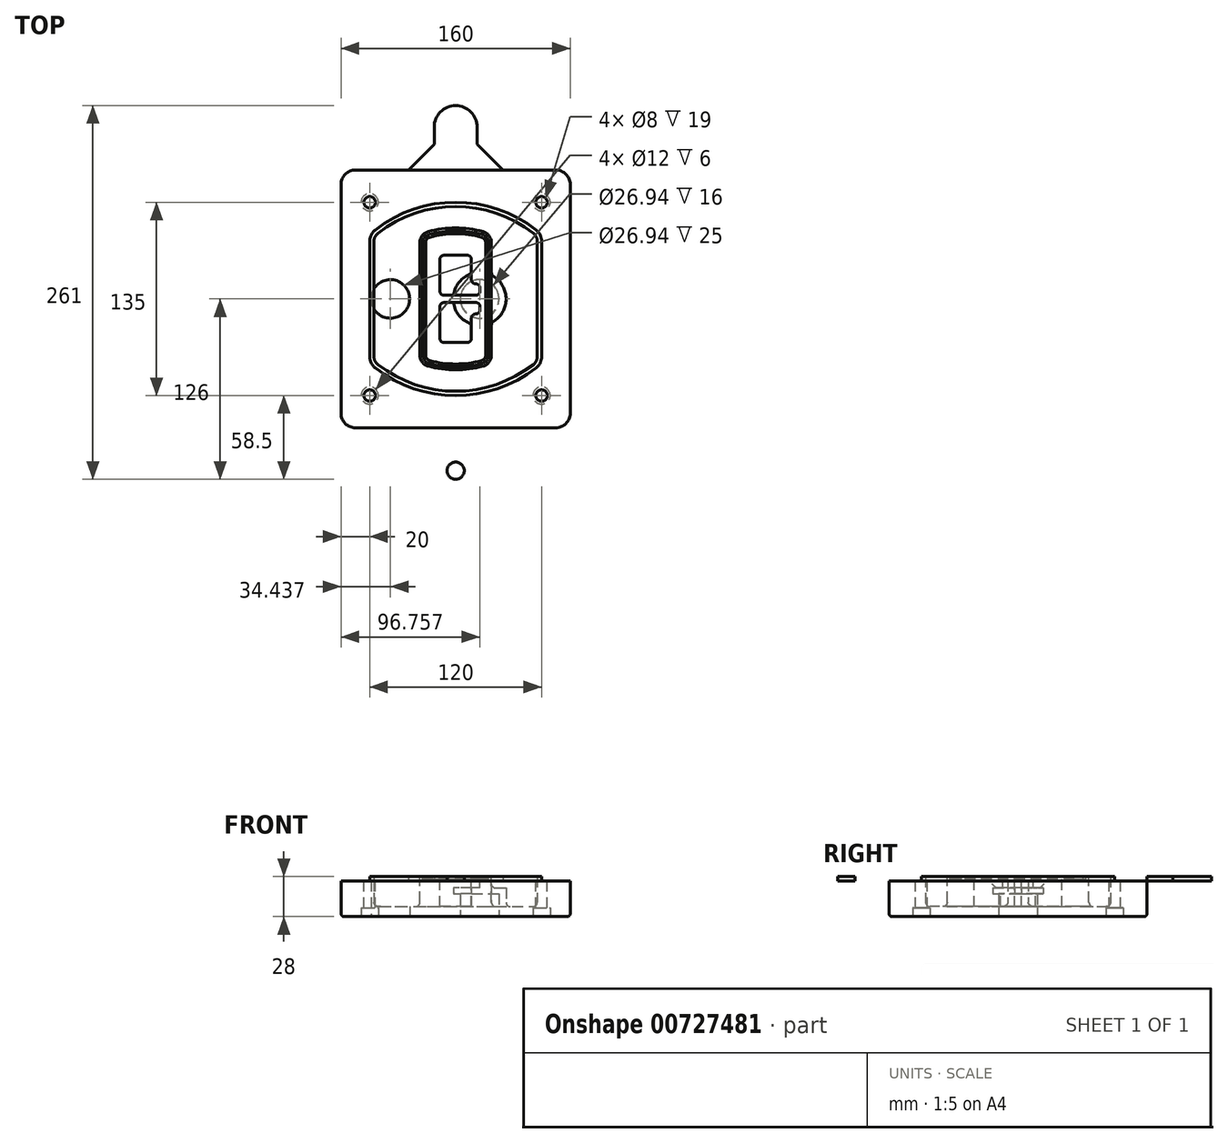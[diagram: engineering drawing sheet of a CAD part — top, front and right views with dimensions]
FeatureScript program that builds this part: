
annotation { "Feature Type Name" : "Feature", "Feature Type Description" : "" }
export const myFeature = defineFeature(function(context is Context, id is Id, definition is map)
    precondition{}
    {
        {
            var Q0;
            Q0=qCreatedBy(makeId("Top.planeOp"),FACE);
            var sketch = newSketch(context, id + "F0", { "sketchPlane" : qUnion([Q0])});
            skPoint(sketch, "E0.rect.middle", {"position": v(0, 0) * mm});
            skLineSegment(sketch, "E1.bottom", {"start": v(-70, -90) * mm, "end": v(70, -90) * mm});
            skLineSegment(sketch, "E1.top", {"start": v(-70, 90) * mm, "end": v(70, 90) * mm});
            skLineSegment(sketch, "E1.left", {"start": v(-80, -80) * mm, "end": v(-80, 80) * mm});
            skLineSegment(sketch, "E1.right", {"start": v(80, -80) * mm, "end": v(80, 80) * mm});
            skLineSegment(sketch, "E2", {"start": v(-80, 90) * mm, "end": v(80, -90) * mm, "construction": true});
            skLineSegment(sketch, "E3", {"start": v(80, 90) * mm, "end": v(-80, -90) * mm, "construction": true});
            skCircle(sketch, "E4", {"center": v(-60, 67.5) * mm, "radius": 4 * mm});
            skCircle(sketch, "E5", {"center": v(60, 67.5) * mm, "radius": 4 * mm});
            skCircle(sketch, "E6", {"center": v(60, -67.5) * mm, "radius": 4 * mm});
            skCircle(sketch, "E7", {"center": v(-60, -67.5) * mm, "radius": 4 * mm});
            skLineSegment(sketch, "E8", {"start": v(-60, 67.5) * mm, "end": v(60, 67.5) * mm, "construction": true});
            skLineSegment(sketch, "E9", {"start": v(60, 67.5) * mm, "end": v(60, -67.5) * mm, "construction": true});
            skLineSegment(sketch, "E10", {"start": v(60, -67.5) * mm, "end": v(-60, -67.5) * mm, "construction": true});
            skLineSegment(sketch, "E11", {"start": v(-60, -67.5) * mm, "end": v(-60, 67.5) * mm, "construction": true});
            skLineSegment(sketch, "E12", {"start": v(-60, 40.3) * mm, "end": v(-60, -40.3) * mm});
            skLineSegment(sketch, "E13", {"start": v(60, 40.3) * mm, "end": v(60, -40.3) * mm});
            skArc(sketch, "E14", {"start": v(56.15, 48.18) * mm, "mid": v(0, 67.5) * mm, "end": v(-56.15, 48.18) * mm});
            skArc(sketch, "E15", {"start": v(-56.15, -48.18) * mm, "mid": v(0, -67.5) * mm, "end": v(56.15, -48.18) * mm});
            skLineSegment(sketch, "E16", {"start": v(-60, 0) * mm, "end": v(60, 0) * mm, "construction": true});
            skPoint(sketch, "E17.visualSharp", {"position": v(-60, -45) * mm});
            skArc(sketch, "E17.filletArc", {"start": v(-60, -40.3) * mm, "mid": v(-58.99, -44.68) * mm, "end": v(-56.15, -48.18) * mm});
            skPoint(sketch, "E18.visualSharp", {"position": v(-60, 45) * mm});
            skArc(sketch, "E18.filletArc", {"start": v(-56.15, 48.18) * mm, "mid": v(-58.99, 44.68) * mm, "end": v(-60, 40.3) * mm});
            skPoint(sketch, "E19.visualSharp", {"position": v(60, 45) * mm});
            skArc(sketch, "E19.filletArc", {"start": v(60, 40.3) * mm, "mid": v(58.99, 44.68) * mm, "end": v(56.15, 48.18) * mm});
            skPoint(sketch, "E20.visualSharp", {"position": v(60, -45) * mm});
            skArc(sketch, "E20.filletArc", {"start": v(56.15, -48.18) * mm, "mid": v(58.99, -44.68) * mm, "end": v(60, -40.3) * mm});
            skPoint(sketch, "E21.visualSharp", {"position": v(-80, 90) * mm});
            skArc(sketch, "E21.filletArc", {"start": v(-70, 90) * mm, "mid": v(-77.07, 87.07) * mm, "end": v(-80, 80) * mm});
            skPoint(sketch, "E22.visualSharp", {"position": v(80, 90) * mm});
            skArc(sketch, "E22.filletArc", {"start": v(80, 80) * mm, "mid": v(77.07, 87.07) * mm, "end": v(70, 90) * mm});
            skPoint(sketch, "E23.visualSharp", {"position": v(80, -90) * mm});
            skArc(sketch, "E23.filletArc", {"start": v(70, -90) * mm, "mid": v(77.07, -87.07) * mm, "end": v(80, -80) * mm});
            skPoint(sketch, "E24.visualSharp", {"position": v(-80, -90) * mm});
            skArc(sketch, "E24.filletArc", {"start": v(-80, -80) * mm, "mid": v(-77.07, -87.07) * mm, "end": v(-70, -90) * mm});
            skArc(sketch, "E25.0", {"start": v(57, 40.3) * mm, "mid": v(56.3, 43.36) * mm, "end": v(54.3, 45.81) * mm});
            skLineSegment(sketch, "E25.1", {"start": v(57, 40.3) * mm, "end": v(57, -40.3) * mm});
            skArc(sketch, "E25.2", {"start": v(54.3, -45.81) * mm, "mid": v(56.3, -43.36) * mm, "end": v(57, -40.3) * mm});
            skArc(sketch, "E25.3", {"start": v(-54.3, -45.81) * mm, "mid": v(0, -64.5) * mm, "end": v(54.3, -45.81) * mm});
            skArc(sketch, "E25.4", {"start": v(-57, -40.3) * mm, "mid": v(-56.3, -43.36) * mm, "end": v(-54.3, -45.81) * mm});
            skArc(sketch, "E25.5", {"start": v(54.3, 45.81) * mm, "mid": v(0, 64.5) * mm, "end": v(-54.3, 45.81) * mm});
            skLineSegment(sketch, "E25.6", {"start": v(-57, 40.3) * mm, "end": v(-57, -40.3) * mm});
            skArc(sketch, "E25.7", {"start": v(-54.3, 45.81) * mm, "mid": v(-56.3, 43.36) * mm, "end": v(-57, 40.3) * mm});
            skArc(sketch, "E26.0", {"start": v(-58.62, 51.33) * mm, "mid": v(-62.58, 46.43) * mm, "end": v(-64, 40.3) * mm});
            skArc(sketch, "E26.1", {"start": v(58.62, 51.33) * mm, "mid": v(0, 71.5) * mm, "end": v(-58.62, 51.33) * mm});
            skArc(sketch, "E26.2", {"start": v(64, 40.3) * mm, "mid": v(62.58, 46.43) * mm, "end": v(58.62, 51.33) * mm});
            skLineSegment(sketch, "E26.3", {"start": v(64, 40.3) * mm, "end": v(64, -40.3) * mm});
            skArc(sketch, "E26.4", {"start": v(58.62, -51.33) * mm, "mid": v(62.58, -46.43) * mm, "end": v(64, -40.3) * mm});
            skLineSegment(sketch, "E26.5", {"start": v(-64, 40.3) * mm, "end": v(-64, -40.3) * mm});
            skArc(sketch, "E26.6", {"start": v(-58.62, -51.33) * mm, "mid": v(0, -71.5) * mm, "end": v(58.62, -51.33) * mm});
            skArc(sketch, "E26.7", {"start": v(-64, -40.3) * mm, "mid": v(-62.58, -46.43) * mm, "end": v(-58.62, -51.33) * mm});
            skSolve(sketch);
        }
        {
            var Q0;
            Q0=makeQuery(id+"F0.imprint","IMPRINT",FACE,{"disambiguationData":[TD([[makeQuery(id+"F0.imprint","IMPRINT",EDGE,{"derivedFrom":sQuery(id+"F0.wireOp",EDGE,"E1.bottom")}),1.0]])]});
            var Q1;
            Q1=makeQuery(id+"F0.imprint","IMPRINT",FACE,{"disambiguationData":[TD([[makeQuery(id+"F0.imprint","IMPRINT",EDGE,{"derivedFrom":sQuery(id+"F0.wireOp",EDGE,"E12")}),1.0]])]});
            var Q2;
            Q2=makeQuery(id+"F0.imprint","IMPRINT",FACE,{"disambiguationData":[TD([[makeQuery(id+"F0.imprint","IMPRINT",EDGE,{"derivedFrom":sQuery(id+"F0.wireOp",EDGE,"E25.0")}),1.0]])]});
            var Q3;
            Q3=makeQuery(id+"F0.imprint","IMPRINT",FACE,{"disambiguationData":[TD([[makeQuery(id+"F0.imprint","IMPRINT",EDGE,{"derivedFrom":sQuery(id+"F0.wireOp",EDGE,"E12")}),-1.0]])]});
            extrude(context, id + "F1", {"entities" : qUnion([Q0, Q1, Q2, Q3]), "oppositeDirection" : true, "depth" : 25 * mm});
        }
        {
            var Q0;
            Q0=makeQuery(id+"F0.imprint","IMPRINT",FACE,{"disambiguationData":[TD([[makeQuery(id+"F0.imprint","IMPRINT",EDGE,{"derivedFrom":sQuery(id+"F0.wireOp",EDGE,"E12")}),1.0]])]});
            extrude(context, id + "F2", {"entities" : qUnion([Q0]), "operationType" : NewBodyOperationType.ADD, "depth" : 3 * mm});
        }
        {
            var Q0;
            Q0=makeQuery(id+"F0.imprint","IMPRINT",FACE,{"disambiguationData":[TD([[makeQuery(id+"F0.imprint","IMPRINT",EDGE,{"derivedFrom":sQuery(id+"F0.wireOp",EDGE,"E25.0")}),1.0]])]});
            extrude(context, id + "F3", {"entities" : qUnion([Q0]), "operationType" : NewBodyOperationType.REMOVE, "oppositeDirection" : true, "depth" : 18 * mm});
        }
        {
            var Q0;
            Q0=makeQuery(id+"F2.opExtrude","CAP_FACE",FACE,{"disambiguationData":[OSD([sQuery(id+"F0.wireOp",EDGE,"E12"),sQuery(id+"F0.wireOp",EDGE,"E13"),sQuery(id+"F0.wireOp",EDGE,"E14"),sQuery(id+"F0.wireOp",EDGE,"E15"),sQuery(id+"F0.wireOp",EDGE,"E17.filletArc"),sQuery(id+"F0.wireOp",EDGE,"E18.filletArc"),sQuery(id+"F0.wireOp",EDGE,"E19.filletArc"),sQuery(id+"F0.wireOp",EDGE,"E20.filletArc"),sQuery(id+"F0.wireOp",EDGE,"E25.0"),sQuery(id+"F0.wireOp",EDGE,"E25.1"),sQuery(id+"F0.wireOp",EDGE,"E25.2"),sQuery(id+"F0.wireOp",EDGE,"E25.3"),sQuery(id+"F0.wireOp",EDGE,"E25.4"),sQuery(id+"F0.wireOp",EDGE,"E25.5"),sQuery(id+"F0.wireOp",EDGE,"E25.6"),sQuery(id+"F0.wireOp",EDGE,"E25.7")])],"isStart":false});
            var sketch = newSketch(context, id + "F4", { "sketchPlane" : qUnion([Q0])});
            skArc(sketch, "E27.0", {"start": v(-19.08, -46.97) * mm, "mid": v(0, -49.5) * mm, "end": v(19.08, -46.97) * mm});
            skArc(sketch, "E28.0", {"start": v(19.08, 46.97) * mm, "mid": v(0, 49.5) * mm, "end": v(-19.08, 46.97) * mm});
            skLineSegment(sketch, "E29", {"start": v(-25, 39.25) * mm, "end": v(-25, -39.25) * mm});
            skLineSegment(sketch, "E30", {"start": v(25, 39.25) * mm, "end": v(25, -39.25) * mm});
            skLineSegment(sketch, "E31", {"start": v(-25, 45.1) * mm, "end": v(25, 45.1) * mm, "construction": true});
            skLineSegment(sketch, "E32", {"start": v(-25, -45.1) * mm, "end": v(25, -45.1) * mm, "construction": true});
            skPoint(sketch, "E33.visualSharp", {"position": v(-25, 45.1) * mm});
            skArc(sketch, "E33.filletArc", {"start": v(-19.08, 46.97) * mm, "mid": v(-23.35, 44.11) * mm, "end": v(-25, 39.25) * mm});
            skPoint(sketch, "E34.visualSharp", {"position": v(25, 45.1) * mm});
            skArc(sketch, "E34.filletArc", {"start": v(25, 39.25) * mm, "mid": v(23.35, 44.11) * mm, "end": v(19.08, 46.97) * mm});
            skPoint(sketch, "E35.visualSharp", {"position": v(25, -45.1) * mm});
            skArc(sketch, "E35.filletArc", {"start": v(19.08, -46.97) * mm, "mid": v(23.35, -44.11) * mm, "end": v(25, -39.25) * mm});
            skPoint(sketch, "E36.visualSharp", {"position": v(-25, -45.1) * mm});
            skArc(sketch, "E36.filletArc", {"start": v(-25, -39.25) * mm, "mid": v(-23.35, -44.11) * mm, "end": v(-19.08, -46.97) * mm});
            skArc(sketch, "E37.0", {"start": v(54.3, 45.81) * mm, "mid": v(0, 64.5) * mm, "end": v(-54.3, 45.81) * mm});
            skArc(sketch, "E37.1", {"start": v(-54.3, 45.81) * mm, "mid": v(-56.3, 43.36) * mm, "end": v(-57, 40.3) * mm});
            skLineSegment(sketch, "E37.2", {"start": v(-57, 40.3) * mm, "end": v(-57, -40.3) * mm});
            skArc(sketch, "E37.3", {"start": v(-57, -40.3) * mm, "mid": v(-56.3, -43.36) * mm, "end": v(-54.3, -45.81) * mm});
            skArc(sketch, "E37.4", {"start": v(-54.3, -45.81) * mm, "mid": v(0, -64.5) * mm, "end": v(54.3, -45.81) * mm});
            skArc(sketch, "E37.5", {"start": v(54.3, -45.81) * mm, "mid": v(56.3, -43.36) * mm, "end": v(57, -40.3) * mm});
            skLineSegment(sketch, "E37.6", {"start": v(57, 40.3) * mm, "end": v(57, -40.3) * mm});
            skArc(sketch, "E37.7", {"start": v(57, 40.3) * mm, "mid": v(56.3, 43.36) * mm, "end": v(54.3, 45.81) * mm});
            skLineSegment(sketch, "E38.0", {"start": v(23, 39.25) * mm, "end": v(23, -39.25) * mm});
            skArc(sketch, "E38.1", {"start": v(18.56, -45.04) * mm, "mid": v(21.76, -42.9) * mm, "end": v(23, -39.25) * mm});
            skArc(sketch, "E38.2", {"start": v(-18.56, -45.04) * mm, "mid": v(0, -47.5) * mm, "end": v(18.56, -45.04) * mm});
            skArc(sketch, "E38.3", {"start": v(-23, -39.25) * mm, "mid": v(-21.76, -42.9) * mm, "end": v(-18.56, -45.04) * mm});
            skLineSegment(sketch, "E38.4", {"start": v(-23, 39.25) * mm, "end": v(-23, -39.25) * mm});
            skArc(sketch, "E38.5", {"start": v(23, 39.25) * mm, "mid": v(21.76, 42.9) * mm, "end": v(18.56, 45.04) * mm});
            skArc(sketch, "E38.6", {"start": v(-18.56, 45.04) * mm, "mid": v(-21.76, 42.9) * mm, "end": v(-23, 39.25) * mm});
            skArc(sketch, "E38.7", {"start": v(18.56, 45.04) * mm, "mid": v(0, 47.5) * mm, "end": v(-18.56, 45.04) * mm});
            skArc(sketch, "E39.0", {"start": v(21, 39.25) * mm, "mid": v(20.18, 41.68) * mm, "end": v(18.04, 43.1) * mm});
            skLineSegment(sketch, "E39.1", {"start": v(21, 39.25) * mm, "end": v(21, -39.25) * mm});
            skArc(sketch, "E39.2", {"start": v(18.04, -43.1) * mm, "mid": v(20.18, -41.68) * mm, "end": v(21, -39.25) * mm});
            skArc(sketch, "E39.3", {"start": v(-18.04, -43.1) * mm, "mid": v(0, -45.5) * mm, "end": v(18.04, -43.1) * mm});
            skArc(sketch, "E39.4", {"start": v(-21, -39.25) * mm, "mid": v(-20.18, -41.68) * mm, "end": v(-18.04, -43.1) * mm});
            skArc(sketch, "E39.5", {"start": v(18.04, 43.1) * mm, "mid": v(0, 45.5) * mm, "end": v(-18.04, 43.1) * mm});
            skLineSegment(sketch, "E39.6", {"start": v(-21, 39.25) * mm, "end": v(-21, -39.25) * mm});
            skArc(sketch, "E39.7", {"start": v(-18.04, 43.1) * mm, "mid": v(-20.18, 41.68) * mm, "end": v(-21, 39.25) * mm});
            skLineSegment(sketch, "E40", {"start": v(-25, 0) * mm, "end": v(25, 0) * mm, "construction": true});
            skLineSegment(sketch, "E41", {"start": v(-11, 5.5) * mm, "end": v(-11, 27.5) * mm});
            skLineSegment(sketch, "E42", {"start": v(-8, 30.5) * mm, "end": v(8, 30.5) * mm});
            skLineSegment(sketch, "E43", {"start": v(11, 27.5) * mm, "end": v(11, 13.5) * mm});
            skLineSegment(sketch, "E44", {"start": v(14, 10.5) * mm, "end": v(14, 10.5) * mm});
            skLineSegment(sketch, "E45", {"start": v(17, 7.5) * mm, "end": v(17, 5.5) * mm});
            skLineSegment(sketch, "E46", {"start": v(14, 2.5) * mm, "end": v(-8, 2.5) * mm});
            skPoint(sketch, "E47.visualSharp", {"position": v(-11, 30.5) * mm});
            skArc(sketch, "E47.filletArc", {"start": v(-8, 30.5) * mm, "mid": v(-10.12, 29.62) * mm, "end": v(-11, 27.5) * mm});
            skPoint(sketch, "E48.visualSharp", {"position": v(11, 30.5) * mm});
            skArc(sketch, "E48.filletArc", {"start": v(11, 27.5) * mm, "mid": v(10.12, 29.62) * mm, "end": v(8, 30.5) * mm});
            skPoint(sketch, "E49.visualSharp", {"position": v(11, 10.5) * mm});
            skArc(sketch, "E49.filletArc", {"start": v(11, 13.5) * mm, "mid": v(11.88, 11.38) * mm, "end": v(14, 10.5) * mm});
            skPoint(sketch, "E50.visualSharp", {"position": v(17, 10.5) * mm});
            skArc(sketch, "E50.filletArc", {"start": v(17, 7.5) * mm, "mid": v(16.12, 9.62) * mm, "end": v(14, 10.5) * mm});
            skPoint(sketch, "E51.visualSharp", {"position": v(17, 2.5) * mm});
            skArc(sketch, "E51.filletArc", {"start": v(14, 2.5) * mm, "mid": v(16.12, 3.38) * mm, "end": v(17, 5.5) * mm});
            skPoint(sketch, "E52.visualSharp", {"position": v(-11, 2.5) * mm});
            skArc(sketch, "E52.filletArc", {"start": v(-11, 5.5) * mm, "mid": v(-10.12, 3.38) * mm, "end": v(-8, 2.5) * mm});
            skLineSegment(sketch, "E53.0.MirrorCS", {"start": v(14, -2.5) * mm, "end": v(-8, -2.5) * mm});
            skArc(sketch, "E54.0.MirrorCS", {"start": v(-11, -5.5) * mm, "mid": v(-10.12, -3.38) * mm, "end": v(-8, -2.5) * mm});
            skLineSegment(sketch, "E55.0.MirrorCS", {"start": v(-11, -5.5) * mm, "end": v(-11, -27.5) * mm});
            skArc(sketch, "E56.0.MirrorCS", {"start": v(-8, -30.5) * mm, "mid": v(-10.12, -29.62) * mm, "end": v(-11, -27.5) * mm});
            skLineSegment(sketch, "E57.0.MirrorCS", {"start": v(-8, -30.5) * mm, "end": v(8, -30.5) * mm});
            skArc(sketch, "E58.0.MirrorCS", {"start": v(11, -27.5) * mm, "mid": v(10.12, -29.62) * mm, "end": v(8, -30.5) * mm});
            skLineSegment(sketch, "E59.0.MirrorCS", {"start": v(11, -27.5) * mm, "end": v(11, -13.5) * mm});
            skArc(sketch, "E60.0.MirrorCS", {"start": v(11, -13.5) * mm, "mid": v(11.88, -11.38) * mm, "end": v(14, -10.5) * mm});
            skArc(sketch, "E61.0.MirrorCS", {"start": v(17, -7.5) * mm, "mid": v(16.12, -9.62) * mm, "end": v(14, -10.5) * mm});
            skLineSegment(sketch, "E62.0.MirrorCS", {"start": v(17, -7.5) * mm, "end": v(17, -5.5) * mm});
            skArc(sketch, "E63.0.MirrorCS", {"start": v(14, -2.5) * mm, "mid": v(16.12, -3.38) * mm, "end": v(17, -5.5) * mm});
            skSolve(sketch);
        }
        {
            var Q0;
            Q0=makeQuery(id+"F4.imprint","IMPRINT",FACE,{"disambiguationData":[TD([[makeQuery(id+"F4.imprint","IMPRINT",EDGE,{"derivedFrom":sQuery(id+"F4.wireOp",EDGE,"E27.0")}),1.0]])]});
            var Q1;
            Q1=makeQuery(id+"F4.imprint","IMPRINT",FACE,{"disambiguationData":[TD([[makeQuery(id+"F4.imprint","IMPRINT",EDGE,{"derivedFrom":sQuery(id+"F4.wireOp",EDGE,"E38.0")}),-1.0]])]});
            var Q2;
            Q2=makeQuery(id+"F4.imprint","IMPRINT",FACE,{"disambiguationData":[TD([[makeQuery(id+"F4.imprint","IMPRINT",EDGE,{"derivedFrom":sQuery(id+"F4.wireOp",EDGE,"E39.0")}),1.0]])]});
            extrude(context, id + "F5", {"entities" : qUnion([Q0, Q1, Q2]), "operationType" : NewBodyOperationType.ADD, "endBound" : BoundingType.UP_TO_NEXT, "oppositeDirection" : true, "depth" : 25 * mm});
        }
        {
            var Q0;
            Q0=makeQuery(id+"F4.imprint","IMPRINT",FACE,{"disambiguationData":[TD([[makeQuery(id+"F4.imprint","IMPRINT",EDGE,{"derivedFrom":sQuery(id+"F4.wireOp",EDGE,"E38.0")}),-1.0]])]});
            extrude(context, id + "F6", {"entities" : qUnion([Q0]), "operationType" : NewBodyOperationType.REMOVE, "oppositeDirection" : true, "depth" : 2 * mm});
        }
        {
            var Q0;
            Q0=makeQuery(id+"F1.opExtrude","CAP_FACE",FACE,{"disambiguationData":[OSD([sQuery(id+"F0.wireOp",EDGE,"E1.bottom"),sQuery(id+"F0.wireOp",EDGE,"E1.top"),sQuery(id+"F0.wireOp",EDGE,"E1.left"),sQuery(id+"F0.wireOp",EDGE,"E1.right"),sQuery(id+"F0.wireOp",EDGE,"E4"),sQuery(id+"F0.wireOp",EDGE,"E5"),sQuery(id+"F0.wireOp",EDGE,"E6"),sQuery(id+"F0.wireOp",EDGE,"E7"),sQuery(id+"F0.wireOp",EDGE,"E21.filletArc"),sQuery(id+"F0.wireOp",EDGE,"E22.filletArc"),sQuery(id+"F0.wireOp",EDGE,"E23.filletArc"),sQuery(id+"F0.wireOp",EDGE,"E24.filletArc")])],"isStart":false});
            var sketch = newSketch(context, id + "F7", { "sketchPlane" : qUnion([Q0])});
            skCircle(sketch, "E64", {"center": v(16.76, 0) * mm, "radius": 13.47 * mm});
            skCircle(sketch, "E65", {"center": v(-45.56, 0) * mm, "radius": 13.47 * mm});
            skLineSegment(sketch, "E66", {"start": v(80, 0) * mm, "end": v(-80, 0) * mm});
            skCircle(sketch, "E67", {"center": v(16.76, 0) * mm, "radius": 18.47 * mm});
            skCircle(sketch, "E68", {"center": v(60, -67.5) * mm, "radius": 6 * mm});
            skCircle(sketch, "E69", {"center": v(-60, -67.5) * mm, "radius": 6 * mm});
            skCircle(sketch, "E70", {"center": v(-60, 67.5) * mm, "radius": 6 * mm});
            skCircle(sketch, "E71", {"center": v(60, 67.5) * mm, "radius": 6 * mm});
            skSolve(sketch);
        }
        {
            var Q0;
            {var subQ1=sQuery(id+"F7.wireOp",EDGE,"E66");var subQ4=sQuery(id+"F7.wireOp",EDGE,"E64");var subQ6=makeQuery(id+"F7.imprint","INTERSECT",VERTEX,{"disambiguationData":[OD(0.0)],"derivedFrom":[subQ4,subQ1]});Q0=makeQuery(id+"F7.imprint","IMPRINT",FACE,{"disambiguationData":[TD([[makeQuery(id+"F7.imprint","IMPRINT",EDGE,{"disambiguationData":[TD([[subQ6,-1.0]])],"derivedFrom":subQ4}),-1.0]])]});}
            var Q1;
            {var subQ0=sQuery(id+"F7.wireOp",EDGE,"E66");var subQ1=sQuery(id+"F7.wireOp",EDGE,"E64");var subQ3=makeQuery(id+"F7.imprint","INTERSECT",VERTEX,{"disambiguationData":[OD(0.0)],"derivedFrom":[subQ1,subQ0]});Q1=makeQuery(id+"F7.imprint","IMPRINT",FACE,{"disambiguationData":[TD([[makeQuery(id+"F7.imprint","IMPRINT",EDGE,{"disambiguationData":[TD([[subQ3,-1.0]])],"derivedFrom":subQ1}),1.0]])]});}
            var Q2;
            {var subQ0=sQuery(id+"F7.wireOp",EDGE,"E66");var subQ1=sQuery(id+"F7.wireOp",EDGE,"E64");var subQ3=makeQuery(id+"F7.imprint","INTERSECT",VERTEX,{"disambiguationData":[OD(0.0)],"derivedFrom":[subQ1,subQ0]});Q2=makeQuery(id+"F7.imprint","IMPRINT",FACE,{"disambiguationData":[TD([[makeQuery(id+"F7.imprint","IMPRINT",EDGE,{"disambiguationData":[TD([[subQ3,1.0]])],"derivedFrom":subQ1}),1.0]])]});}
            var Q3;
            {var subQ1=sQuery(id+"F7.wireOp",EDGE,"E66");var subQ4=sQuery(id+"F7.wireOp",EDGE,"E64");var subQ6=makeQuery(id+"F7.imprint","INTERSECT",VERTEX,{"disambiguationData":[OD(0.0)],"derivedFrom":[subQ4,subQ1]});Q3=makeQuery(id+"F7.imprint","IMPRINT",FACE,{"disambiguationData":[TD([[makeQuery(id+"F7.imprint","IMPRINT",EDGE,{"disambiguationData":[TD([[subQ6,1.0]])],"derivedFrom":subQ4}),-1.0]])]});}
            extrude(context, id + "F8", {"entities" : qUnion([Q0, Q1, Q2, Q3]), "operationType" : NewBodyOperationType.ADD, "oppositeDirection" : true, "depth" : 20 * mm});
        }
        {
            var Q0;
            {var subQ0=sQuery(id+"F7.wireOp",EDGE,"E66");var subQ1=sQuery(id+"F7.wireOp",EDGE,"E64");var subQ3=makeQuery(id+"F7.imprint","INTERSECT",VERTEX,{"disambiguationData":[OD(0.0)],"derivedFrom":[subQ1,subQ0]});Q0=makeQuery(id+"F7.imprint","IMPRINT",FACE,{"disambiguationData":[TD([[makeQuery(id+"F7.imprint","IMPRINT",EDGE,{"disambiguationData":[TD([[subQ3,-1.0]])],"derivedFrom":subQ1}),1.0]])]});}
            var Q1;
            {var subQ0=sQuery(id+"F7.wireOp",EDGE,"E66");var subQ1=sQuery(id+"F7.wireOp",EDGE,"E64");var subQ3=makeQuery(id+"F7.imprint","INTERSECT",VERTEX,{"disambiguationData":[OD(0.0)],"derivedFrom":[subQ1,subQ0]});Q1=makeQuery(id+"F7.imprint","IMPRINT",FACE,{"disambiguationData":[TD([[makeQuery(id+"F7.imprint","IMPRINT",EDGE,{"disambiguationData":[TD([[subQ3,1.0]])],"derivedFrom":subQ1}),1.0]])]});}
            extrude(context, id + "F9", {"entities" : qUnion([Q0, Q1]), "operationType" : NewBodyOperationType.REMOVE, "oppositeDirection" : true, "depth" : 16 * mm});
        }
        {
            var Q0;
            {var subQ0=sQuery(id+"F7.wireOp",EDGE,"E66");var subQ1=sQuery(id+"F7.wireOp",EDGE,"E65");var subQ3=makeQuery(id+"F7.imprint","INTERSECT",VERTEX,{"disambiguationData":[OD(0.0)],"derivedFrom":[subQ1,subQ0]});Q0=makeQuery(id+"F7.imprint","IMPRINT",FACE,{"disambiguationData":[TD([[makeQuery(id+"F7.imprint","IMPRINT",EDGE,{"disambiguationData":[TD([[subQ3,-1.0]])],"derivedFrom":subQ1}),1.0]])]});}
            var Q1;
            {var subQ0=sQuery(id+"F7.wireOp",EDGE,"E66");var subQ1=sQuery(id+"F7.wireOp",EDGE,"E65");var subQ3=makeQuery(id+"F7.imprint","INTERSECT",VERTEX,{"disambiguationData":[OD(0.0)],"derivedFrom":[subQ1,subQ0]});Q1=makeQuery(id+"F7.imprint","IMPRINT",FACE,{"disambiguationData":[TD([[makeQuery(id+"F7.imprint","IMPRINT",EDGE,{"disambiguationData":[TD([[subQ3,1.0]])],"derivedFrom":subQ1}),1.0]])]});}
            extrude(context, id + "F10", {"entities" : qUnion([Q0, Q1]), "operationType" : NewBodyOperationType.REMOVE, "oppositeDirection" : true, "depth" : 25 * mm});
        }
        {
            var Q0;
            Q0=makeQuery(id+"F7.imprint","IMPRINT",FACE,{"disambiguationData":[TD([[makeQuery(id+"F7.imprint","IMPRINT",EDGE,{"derivedFrom":sQuery(id+"F7.wireOp",EDGE,"E68")}),1.0]])]});
            var Q1;
            Q1=makeQuery(id+"F7.imprint","IMPRINT",FACE,{"disambiguationData":[TD([[makeQuery(id+"F7.imprint","IMPRINT",EDGE,{"derivedFrom":makeQuery(id+"F1.opExtrude","CAP_EDGE",EDGE,{"disambiguationData":[OSD([sQuery(id+"F0.wireOp",EDGE,"E5")])],"isStart":false})}),-1.0]])]});
            var Q2;
            Q2=makeQuery(id+"F7.imprint","IMPRINT",FACE,{"disambiguationData":[TD([[makeQuery(id+"F7.imprint","IMPRINT",EDGE,{"derivedFrom":sQuery(id+"F7.wireOp",EDGE,"E69")}),1.0]])]});
            var Q3;
            Q3=makeQuery(id+"F7.imprint","IMPRINT",FACE,{"disambiguationData":[TD([[makeQuery(id+"F7.imprint","IMPRINT",EDGE,{"derivedFrom":makeQuery(id+"F1.opExtrude","CAP_EDGE",EDGE,{"disambiguationData":[OSD([sQuery(id+"F0.wireOp",EDGE,"E4")])],"isStart":false})}),-1.0]])]});
            var Q4;
            Q4=makeQuery(id+"F7.imprint","IMPRINT",FACE,{"disambiguationData":[TD([[makeQuery(id+"F7.imprint","IMPRINT",EDGE,{"derivedFrom":sQuery(id+"F7.wireOp",EDGE,"E70")}),1.0]])]});
            var Q5;
            Q5=makeQuery(id+"F7.imprint","IMPRINT",FACE,{"disambiguationData":[TD([[makeQuery(id+"F7.imprint","IMPRINT",EDGE,{"derivedFrom":makeQuery(id+"F1.opExtrude","CAP_EDGE",EDGE,{"disambiguationData":[OSD([sQuery(id+"F0.wireOp",EDGE,"E7")])],"isStart":false})}),-1.0]])]});
            var Q6;
            Q6=makeQuery(id+"F7.imprint","IMPRINT",FACE,{"disambiguationData":[TD([[makeQuery(id+"F7.imprint","IMPRINT",EDGE,{"derivedFrom":sQuery(id+"F7.wireOp",EDGE,"E71")}),1.0]])]});
            var Q7;
            Q7=makeQuery(id+"F7.imprint","IMPRINT",FACE,{"disambiguationData":[TD([[makeQuery(id+"F7.imprint","IMPRINT",EDGE,{"derivedFrom":makeQuery(id+"F1.opExtrude","CAP_EDGE",EDGE,{"disambiguationData":[OSD([sQuery(id+"F0.wireOp",EDGE,"E6")])],"isStart":false})}),-1.0]])]});
            extrude(context, id + "F11", {"entities" : qUnion([Q0, Q1, Q2, Q3, Q4, Q5, Q6, Q7]), "operationType" : NewBodyOperationType.REMOVE, "oppositeDirection" : true, "depth" : 6 * mm});
        }
        {
            var Q0;
            Q0=makeQuery(id+"F9.boolean.opBoolean","COPY",FACE,{"derivedFrom":makeQuery(id+"F9.opExtrude","CAP_FACE",FACE,{"disambiguationData":[OSD([sQuery(id+"F7.wireOp",EDGE,"E64")])],"isStart":false})});
            var sketch = newSketch(context, id + "F12", { "sketchPlane" : qUnion([Q0])});
            skArc(sketch, "E72.0", {"start": v(11, 17.55) * mm, "mid": v(2.57, 11.82) * mm, "end": v(-1.54, 2.5) * mm});
            skArc(sketch, "E72.1", {"start": v(-1.54, -2.5) * mm, "mid": v(2.57, -11.82) * mm, "end": v(11, -17.55) * mm});
            skLineSegment(sketch, "E73", {"start": v(-1.54, -2.5) * mm, "end": v(14, -2.5) * mm});
            skLineSegment(sketch, "E74.0", {"start": v(14, 2.5) * mm, "end": v(-1.54, 2.5) * mm});
            skArc(sketch, "E74.1", {"start": v(14, 2.5) * mm, "mid": v(16.12, 3.38) * mm, "end": v(17, 5.5) * mm});
            skLineSegment(sketch, "E74.2", {"start": v(17, 7.5) * mm, "end": v(17, 5.5) * mm});
            skArc(sketch, "E74.3", {"start": v(17, 7.5) * mm, "mid": v(16.12, 9.62) * mm, "end": v(14, 10.5) * mm});
            skArc(sketch, "E74.4", {"start": v(11, 13.5) * mm, "mid": v(11.88, 11.38) * mm, "end": v(14, 10.5) * mm});
            skLineSegment(sketch, "E74.5", {"start": v(11, 17.55) * mm, "end": v(11, 13.5) * mm});
            skLineSegment(sketch, "E74.7", {"start": v(14, -2.5) * mm, "end": v(-1.54, -2.5) * mm});
            skArc(sketch, "E74.8", {"start": v(14, -2.5) * mm, "mid": v(16.12, -3.38) * mm, "end": v(17, -5.5) * mm});
            skLineSegment(sketch, "E74.9", {"start": v(17, -7.5) * mm, "end": v(17, -5.5) * mm});
            skArc(sketch, "E74.10", {"start": v(17, -7.5) * mm, "mid": v(16.12, -9.62) * mm, "end": v(14, -10.5) * mm});
            skArc(sketch, "E74.11", {"start": v(11, -13.5) * mm, "mid": v(11.88, -11.38) * mm, "end": v(14, -10.5) * mm});
            skLineSegment(sketch, "E74.12", {"start": v(11, -17.55) * mm, "end": v(11, -13.5) * mm});
            skPoint(sketch, "E75.orphan", {"position": v(11, -27.5) * mm});
            skPoint(sketch, "E76.orphan", {"position": v(-8, -2.5) * mm});
            skPoint(sketch, "E77.orphan", {"position": v(-8, 2.5) * mm});
            skPoint(sketch, "E78.orphan", {"position": v(11, 27.5) * mm});
            skSolve(sketch);
        }
        {
            var Q0;
            {var subQ7=sQuery(id+"F12.wireOp",EDGE,"E72.0");var subQ14=sQuery(id+"F12.wireOp",EDGE,"E72.1");var subQ16=sQuery(id+"F12.wireOp",EDGE,"E74.1");var subQ18=sQuery(id+"F12.wireOp",EDGE,"E74.8");Q0=qUnion([makeQuery(id+"F12.imprint","IMPRINT",FACE,{"disambiguationData":[TD([[makeQuery(id+"F12.imprint","IMPRINT",EDGE,{"derivedFrom":subQ7}),1.0]])]}),makeQuery(id+"F12.imprint","IMPRINT",FACE,{"disambiguationData":[TD([[makeQuery(id+"F12.imprint","IMPRINT",EDGE,{"derivedFrom":subQ14}),1.0]])]}),makeQuery(id+"F12.imprint","IMPRINT",FACE,{"disambiguationData":[TD([[makeQuery(id+"F12.imprint","IMPRINT",EDGE,{"derivedFrom":subQ16}),1.0]])]}),makeQuery(id+"F12.imprint","IMPRINT",FACE,{"disambiguationData":[TD([[makeQuery(id+"F12.imprint","IMPRINT",EDGE,{"derivedFrom":subQ18}),-1.0]])]})]);}
            var Q1;
            Q1=makeQuery(id+"F5.boolean.opBoolean","SPLIT",FACE,{"disambiguationData":[TD([makeQuery(id+"F5.opExtrude","SWEPT_FACE",FACE,{"disambiguationData":[OSD([sQuery(id+"F4.wireOp",EDGE,"E41")])]})])],"derivedFrom":makeQuery(id+"F3.boolean.opBoolean","COPY",FACE,{"derivedFrom":makeQuery(id+"F3.opExtrude","CAP_FACE",FACE,{"disambiguationData":[OSD([sQuery(id+"F0.wireOp",EDGE,"E25.0"),sQuery(id+"F0.wireOp",EDGE,"E25.1"),sQuery(id+"F0.wireOp",EDGE,"E25.2"),sQuery(id+"F0.wireOp",EDGE,"E25.3"),sQuery(id+"F0.wireOp",EDGE,"E25.4"),sQuery(id+"F0.wireOp",EDGE,"E25.5"),sQuery(id+"F0.wireOp",EDGE,"E25.6"),sQuery(id+"F0.wireOp",EDGE,"E25.7")])],"isStart":false})})});
            extrude(context, id + "F13", {"entities" : qUnion([Q0]), "operationType" : NewBodyOperationType.REMOVE, "endBound" : BoundingType.UP_TO_SURFACE, "endBoundEntityFace" : qUnion([Q1]), "depth" : 25 * mm});
        }
        {
            var Q0;
            Q0=makeQuery(id+"F3.boolean.opBoolean","COPY",EDGE,{"derivedFrom":makeQuery(id+"F3.opExtrude","CAP_EDGE",EDGE,{"disambiguationData":[OSD([sQuery(id+"F0.wireOp",EDGE,"E25.6")])],"isStart":false})});
            var Q1;
            Q1=makeQuery(id+"F8.boolean.opBoolean","INTERSECT",EDGE,{"derivedFrom":[makeQuery(id+"F5.opExtrude","SWEPT_FACE",FACE,{"disambiguationData":[OSD([sQuery(id+"F4.wireOp",EDGE,"E30")])]}),makeQuery(id+"F8.opExtrude","CAP_FACE",FACE,{"disambiguationData":[OSD([sQuery(id+"F7.wireOp",EDGE,"E67")])],"isStart":false})]});
            var Q2;
            Q2=makeQuery(id+"F8.boolean.opBoolean","INTERSECT",EDGE,{"disambiguationData":[OD(1.0)],"derivedFrom":[makeQuery(id+"F5.opExtrude","SWEPT_FACE",FACE,{"disambiguationData":[OSD([sQuery(id+"F4.wireOp",EDGE,"E30")])]}),makeQuery(id+"F8.opExtrude","SWEPT_FACE",FACE,{"disambiguationData":[OSD([sQuery(id+"F7.wireOp",EDGE,"E67")])]})]});
            var Q3;
            {var subQ0=sQuery(id+"F4.wireOp",EDGE,"E30");Q3=makeQuery(id+"F8.boolean.opBoolean","SPLIT",EDGE,{"disambiguationData":[TD([makeQuery(id+"F5.opExtrude","SWEPT_FACE",FACE,{"disambiguationData":[OSD([sQuery(id+"F4.wireOp",EDGE,"E35.filletArc")])]})])],"derivedFrom":makeQuery(id+"F5.opExtrude","CAP_EDGE",EDGE,{"disambiguationData":[OSD([subQ0])],"isStart":false})});}
            var Q4;
            {var subQ0=sQuery(id+"F0.wireOp",EDGE,"E25.7");var subQ1=sQuery(id+"F0.wireOp",EDGE,"E25.1");var subQ2=sQuery(id+"F0.wireOp",EDGE,"E25.6");var subQ3=sQuery(id+"F0.wireOp",EDGE,"E25.5");var subQ4=sQuery(id+"F0.wireOp",EDGE,"E25.4");var subQ5=sQuery(id+"F0.wireOp",EDGE,"E25.0");var subQ6=sQuery(id+"F0.wireOp",EDGE,"E25.2");var subQ7=sQuery(id+"F0.wireOp",EDGE,"E25.3");Q4=makeQuery(id+"F8.boolean.opBoolean","INTERSECT",EDGE,{"derivedFrom":[makeQuery(id+"F5.boolean.opBoolean","SPLIT",FACE,{"disambiguationData":[TD([makeQuery(id+"F2.opExtrude","SWEPT_FACE",FACE,{"disambiguationData":[OSD([subQ5])]})])],"derivedFrom":makeQuery(id+"F3.boolean.opBoolean","COPY",FACE,{"derivedFrom":makeQuery(id+"F3.opExtrude","CAP_FACE",FACE,{"disambiguationData":[OSD([subQ5,subQ1,subQ6,subQ7,subQ4,subQ3,subQ2,subQ0])],"isStart":false})})}),makeQuery(id+"F8.opExtrude","SWEPT_FACE",FACE,{"disambiguationData":[OSD([sQuery(id+"F7.wireOp",EDGE,"E67")])]})]});}
            var Q5;
            Q5=makeQuery(id+"F8.boolean.opBoolean","INTERSECT",EDGE,{"disambiguationData":[OD(0.0)],"derivedFrom":[makeQuery(id+"F5.opExtrude","SWEPT_FACE",FACE,{"disambiguationData":[OSD([sQuery(id+"F4.wireOp",EDGE,"E30")])]}),makeQuery(id+"F8.opExtrude","SWEPT_FACE",FACE,{"disambiguationData":[OSD([sQuery(id+"F7.wireOp",EDGE,"E67")])]})]});
            fillet(context, id + "F14", {"entities" : qUnion([Q0, Q1, Q2, Q3, Q4, Q5]), "radius" : 3 * mm, "tangentPropagation" : true, "allowEdgeOverflow" : false});
        }
        {
            var Q0;
            Q0=makeQuery(id+"F1.opExtrude","CAP_EDGE",EDGE,{"disambiguationData":[OSD([sQuery(id+"F0.wireOp",EDGE,"E1.bottom")])],"isStart":false});
            fillet(context, id + "F15", {"entities" : qUnion([Q0]), "radius" : 2 * mm, "tangentPropagation" : true, "allowEdgeOverflow" : false});
        }
        {
            var Q0;
            {var subQ0=sQuery(id+"F0.wireOp",EDGE,"E21.filletArc");var subQ1=sQuery(id+"F0.wireOp",EDGE,"E7");var subQ2=sQuery(id+"F0.wireOp",EDGE,"E6");var subQ3=sQuery(id+"F0.wireOp",EDGE,"E5");var subQ4=sQuery(id+"F0.wireOp",EDGE,"E4");var subQ5=sQuery(id+"F0.wireOp",EDGE,"E22.filletArc");var subQ6=sQuery(id+"F0.wireOp",EDGE,"E1.bottom");var subQ7=sQuery(id+"F0.wireOp",EDGE,"E1.right");var subQ8=sQuery(id+"F0.wireOp",EDGE,"E1.top");var subQ9=sQuery(id+"F0.wireOp",EDGE,"E1.left");var subQ10=sQuery(id+"F0.wireOp",EDGE,"E23.filletArc");var subQ11=sQuery(id+"F0.wireOp",EDGE,"E24.filletArc");Q0=makeQuery(id+"F2.boolean.opBoolean","SPLIT",FACE,{"disambiguationData":[TD([makeQuery(id+"F1.opExtrude","SWEPT_FACE",FACE,{"disambiguationData":[OSD([subQ6])]})])],"derivedFrom":makeQuery(id+"F1.opExtrude","CAP_FACE",FACE,{"disambiguationData":[OSD([subQ6,subQ8,subQ9,subQ7,subQ4,subQ3,subQ2,subQ1,subQ0,subQ5,subQ10,subQ11])],"isStart":true})});}
            var sketch = newSketch(context, id + "F16", { "sketchPlane" : qUnion([Q0])});
            skLineSegment(sketch, "E79", {"start": v(-33, 90) * mm, "end": v(-15, 108) * mm});
            skLineSegment(sketch, "E80", {"start": v(-15, 108) * mm, "end": v(-15, 120) * mm});
            skLineSegment(sketch, "E81", {"start": v(-15, 120) * mm, "end": v(-15, 108) * mm});
            skLineSegment(sketch, "E82", {"start": v(33, 90) * mm, "end": v(15, 108) * mm});
            skLineSegment(sketch, "E83", {"start": v(15, 108) * mm, "end": v(15, 120) * mm});
            skLineSegment(sketch, "E84", {"start": v(15, 120) * mm, "end": v(15, 108) * mm});
            skArc(sketch, "E85", {"start": v(15, 120) * mm, "mid": v(0, 135) * mm, "end": v(-15, 120) * mm});
            skCircle(sketch, "E86", {"center": v(0, 120) * mm, "radius": 6 * mm});
            skPoint(sketch, "E87.orphan", {"position": v(0, 90) * mm});
            skLineSegment(sketch, "E88", {"start": v(-80, 0) * mm, "end": v(80, 0) * mm});
            skLineSegment(sketch, "E89", {"start": v(80, 0) * mm, "end": v(-80, 0) * mm, "construction": true});
            skArc(sketch, "E90.MirrorCS", {"start": v(15, -120) * mm, "mid": v(0, -135) * mm, "end": v(-15, -120) * mm});
            skCircle(sketch, "E91.MirrorC", {"center": v(0, -120) * mm, "radius": 6 * mm});
            skLineSegment(sketch, "E92.MirrorCS", {"start": v(15, -120) * mm, "end": v(15, -108) * mm});
            skLineSegment(sketch, "E93.MirrorCS", {"start": v(-15, -120) * mm, "end": v(-15, -108) * mm});
            skLineSegment(sketch, "E94.MirrorCS", {"start": v(-33, -90) * mm, "end": v(-15, -108) * mm});
            skLineSegment(sketch, "E95.MirrorCS", {"start": v(33, -90) * mm, "end": v(15, -108) * mm});
            skPoint(sketch, "E96.orphan", {"position": v(0, -90) * mm});
            skLineSegment(sketch, "E97", {"start": v(0, 90) * mm, "end": v(0, 120) * mm, "construction": true});
            skSolve(sketch);
        }
        {
            var Q0;
            Q0 = qSketchRegion(id + "F16", true);
            var Q1;
            {var subQ1=sQuery(id+"F16.wireOp",EDGE,"E79");Q1=makeQuery(id+"F16.imprint","IMPRINT",FACE,{"disambiguationData":[TD([[makeQuery(id+"F16.imprint","IMPRINT",EDGE,{"derivedFrom":subQ1}),-1.0]])]});}
            var Q2;
            Q2=makeQuery(id+"F16.imprint","IMPRINT",FACE,{"disambiguationData":[TD([[makeQuery(id+"F16.imprint","IMPRINT",EDGE,{"derivedFrom":sQuery(id+"F16.wireOp",EDGE,"E90.MirrorCS")}),-1.0]])]});
            var Q3;
            Q3=makeQuery(id+"F2.opExtrude","CAP_FACE",FACE,{"disambiguationData":[OSD([sQuery(id+"F0.wireOp",EDGE,"E12"),sQuery(id+"F0.wireOp",EDGE,"E13"),sQuery(id+"F0.wireOp",EDGE,"E14"),sQuery(id+"F0.wireOp",EDGE,"E15"),sQuery(id+"F0.wireOp",EDGE,"E17.filletArc"),sQuery(id+"F0.wireOp",EDGE,"E18.filletArc"),sQuery(id+"F0.wireOp",EDGE,"E19.filletArc"),sQuery(id+"F0.wireOp",EDGE,"E20.filletArc"),sQuery(id+"F0.wireOp",EDGE,"E25.0"),sQuery(id+"F0.wireOp",EDGE,"E25.1"),sQuery(id+"F0.wireOp",EDGE,"E25.2"),sQuery(id+"F0.wireOp",EDGE,"E25.3"),sQuery(id+"F0.wireOp",EDGE,"E25.4"),sQuery(id+"F0.wireOp",EDGE,"E25.5"),sQuery(id+"F0.wireOp",EDGE,"E25.6"),sQuery(id+"F0.wireOp",EDGE,"E25.7")])],"isStart":false});
            extrude(context, id + "F17", {"entities" : qUnion([Q0, Q1, Q2]), "endBound" : BoundingType.UP_TO_SURFACE, "depth" : 25 * mm, "endBoundEntityFace" : qUnion([Q3]), "offsetDistance" : 25 * mm});
        }
    });
